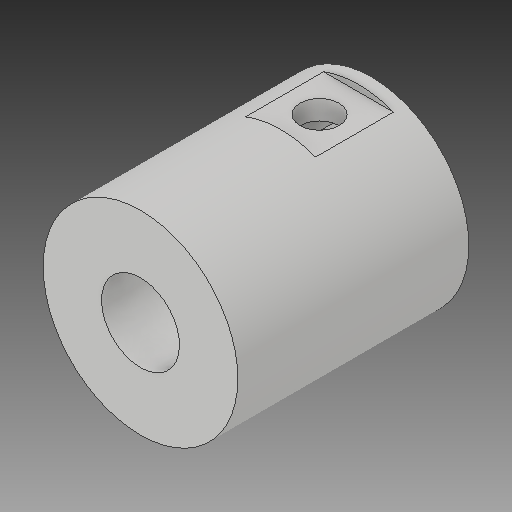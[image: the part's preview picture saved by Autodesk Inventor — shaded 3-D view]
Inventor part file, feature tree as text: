
AUTODESK INVENTOR PART (.ipt)
format: ipt  version: 2019 (Build 230136000, 136)  size: 141,312 bytes
history: native  units: mm
features: extrude x4, sketch x4, plane x1
ambient origin geometry x8: Origin, YZ Plane, XZ Plane, XY Plane, X Axis, Y Axis, Z Axis, Center Point
bodies: Solid1 (feature_tree)
feature tree (9):
  extrude  "Extrusion1"  Depth=6.0mm
  plane  "Work Plane1"
  extrude  "Extrusion2"  Depth=5.0mm
  extrude  "Extrusion3"  Depth=2.2mm
  extrude  "Extrusion4"  Depth=10.0mm TaperAngle=0.0deg
  sketch  "Sketch1"  dims[d0=15.0mm d1=6.0mm]
  sketch  "Sketch2"  dims[d2=17.8mm d3=0.0mm d4=5.0mm]
  sketch  "Sketch4"  dims[d5=5.5mm d6=2.2mm]
  sketch  "Sketch5"  dims[d7=5.2mm d8=10.0mm d9=0.0mm d12=3.0mm d13=4.0mm d14=8.0mm d15=0.0mm d16=6.0mm d17=7.0mm d18=0.5mm d19=8.0mm d20=0.0mm]
